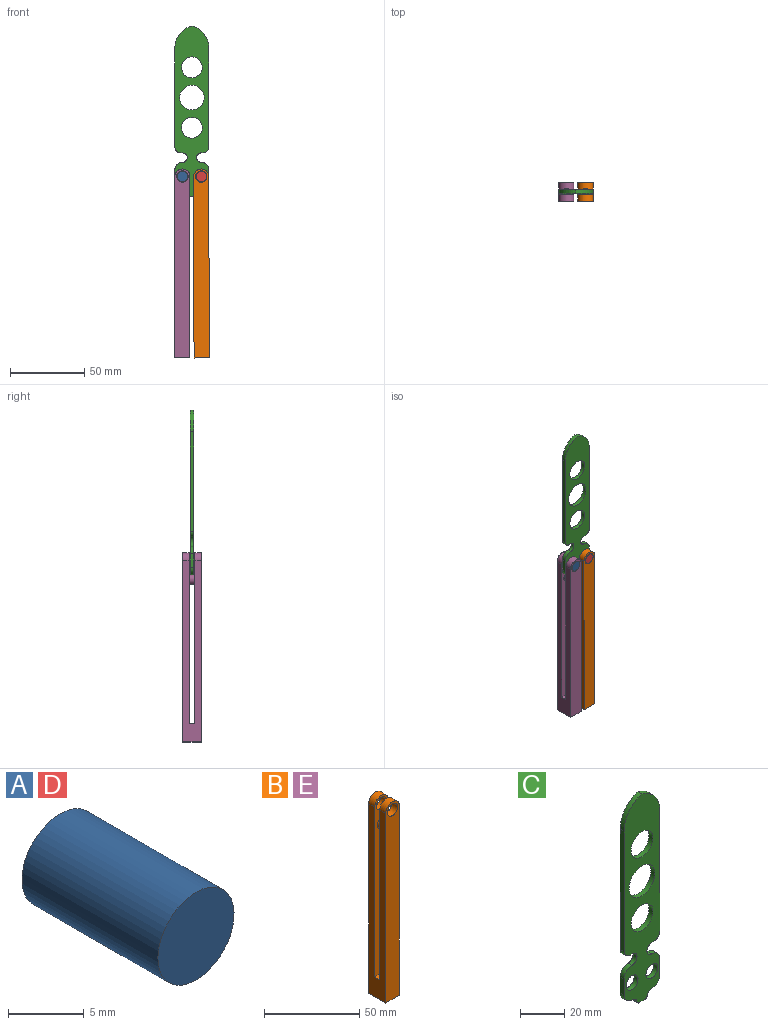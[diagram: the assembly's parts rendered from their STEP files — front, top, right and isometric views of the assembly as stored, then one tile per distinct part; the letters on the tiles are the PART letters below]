
ASSEMBLY  parts=5 mates=4
PART A: 3 faces, bbox 7.1x12.7x7.1 mm
  f0: cylinder r=3.56mm len=12.7mm, axis (0,-1,0), area 283.8mm2, adj f1,f2
  f1: plane 7.11x7.11mm, normal (0,1,0), area 39.7mm2, adj f0
  f2: plane 7.11x7.11mm, normal (0,-1,0), area 39.7mm2, adj f0
PART B: 13 faces, bbox 10.2x12.7x127 mm
  f0: plane 12.7x10.16mm, normal (0,0,-1), area 129mm2, adj f1,f2,f8,f9
  f1: plane 127x10.16mm, normal (0,1,0), area 1233.6mm2, adj f0,f7,f8,f9,f10
  f2: plane 127x10.16mm, normal (0,-1,0), area 1233.6mm2, adj f0,f6,f8,f9,f11
  f3: plane 114.3x10.16mm, normal (0,-1,0), area 1072.9mm2, adj f5,f7,f8,f9,f10,f12
  f4: plane 114.3x10.16mm, normal (0,1,0), area 1072.9mm2, adj f5,f6,f8,f9,f11,f12
  f5: plane 10.16x3.81mm, normal (0,0,1), area 38.7mm2, adj f3,f4,f8,f9
  f6: cylinder r=3.81mm len=7.62mm, axis (0,-1,0), area 106.4mm2, adj f2,f4
  f7: cylinder r=3.81mm len=7.62mm, axis (0,-1,0), area 106.4mm2, adj f1,f3
  f8: plane 121.92x12.7mm, normal (1,0,0), area 1132.3mm2, adj f0,f1,f2,f3,f4,f5,f10,f11
  f9: plane 121.92x12.7mm, normal (-1,0,0), area 1132.3mm2, adj f0,f1,f2,f3,f4,f5,f10,f11
  f10: cylinder r=5.08mm len=10.16mm, axis (0,1,0), area 70.9mm2, adj f1,f3,f8,f9
  f11: cylinder r=5.08mm len=10.16mm, axis (0,-1,0), area 70.9mm2, adj f2,f4,f8,f9
  f12: cylinder r=3.17mm len=6.35mm, axis (0,-1,0), area 76mm2, adj f3,f4
PART C: 28 faces, bbox 22.9x2.5x114.5 mm
  f0: cylinder r=3.17mm len=3.14mm, axis (0,-1,0), area 11.5mm2, adj f3,f4,f17,f20
  f1: plane 8.89x2.54mm, normal (-1,0,0), area 22.6mm2, adj f3,f4,f19,f22
  f2: plane 8.89x2.54mm, normal (1,0,0), area 22.6mm2, adj f3,f4,f20,f21
  f3: plane 114.45x22.86mm, normal (0,1,0), area 1733.4mm2, adj f0,f1,f2,f5,f6,f7,f8,f9
  f4: plane 114.45x22.86mm, normal (0,-1,0), area 1733.4mm2, adj f0,f1,f2,f5,f6,f7,f8,f9
  f5: plane 66.68x2.54mm, normal (-1,0,0), area 169.4mm2, adj f3,f4,f7,f24
  f6: plane 66.68x2.54mm, normal (1,0,0), area 169.4mm2, adj f3,f4,f8,f23
  f7: cylinder r=15.24mm len=14.76mm, axis (0,-1,0), area 51mm2, adj f3,f4,f5,f8
  f8: cylinder r=15.24mm len=14.76mm, axis (0,1,0), area 51mm2, adj f3,f4,f6,f7
  f9: cylinder r=3.81mm len=7.62mm, axis (0,-1,0), area 60.8mm2, adj f3,f4
  f10: cylinder r=3.81mm len=7.62mm, axis (0,-1,0), area 60.8mm2, adj f3,f4
  f11: plane 2.54x1.27mm, normal (0,0,-1), area 3.2mm2, adj f3,f4,f12,f24
  f12: cylinder r=3.17mm len=6.35mm, axis (0,-1,0), area 25.3mm2, adj f3,f4,f11,f22
  f13: plane 2.54x1.27mm, normal (0,0,-1), area 3.2mm2, adj f3,f4,f14,f23
  f14: cylinder r=3.17mm len=6.35mm, axis (0,-1,0), area 25.3mm2, adj f3,f4,f13,f21
  f15: cylinder r=3.17mm len=3.14mm, axis (0,-1,0), area 11.5mm2, adj f3,f4,f18,f19
  f16: plane 3.9x2.54mm, normal (0,0,-1), area 9.9mm2, adj f3,f4,f17,f18
  f17: cylinder r=1.27mm len=2.54mm, axis (0,-1,0), area 4.6mm2, adj f0,f3,f4,f16
  f18: cylinder r=1.27mm len=2.54mm, axis (0,-1,0), area 4.6mm2, adj f3,f4,f15,f16
  f19: cylinder r=5.08mm len=5.08mm, axis (0,-1,0), area 20.3mm2, adj f1,f3,f4,f15
  f20: cylinder r=5.08mm len=5.08mm, axis (0,-1,0), area 20.3mm2, adj f0,f2,f3,f4
  f21: cylinder r=5.08mm len=5.08mm, axis (0,1,0), area 20.3mm2, adj f2,f3,f4,f14
  f22: cylinder r=5.08mm len=5.08mm, axis (0,1,0), area 20.3mm2, adj f1,f3,f4,f12
  f23: cylinder r=3.81mm len=3.81mm, axis (0,-1,0), area 15.2mm2, adj f3,f4,f6,f13
  f24: cylinder r=3.81mm len=3.81mm, axis (0,-1,0), area 15.2mm2, adj f3,f4,f5,f11
  f25: cylinder r=6.99mm len=13.97mm, axis (0,-1,0), area 111.5mm2, adj f3,f4
  f26: cylinder r=8.26mm len=16.51mm, axis (0,-1,0), area 131.7mm2, adj f3,f4
  f27: cylinder r=6.99mm len=13.97mm, axis (0,-1,0), area 111.5mm2, adj f3,f4
PART D: same geometry as A
PART E: same geometry as B
PLACE A t=(20.78,1.06,12.73)mm
PLACE B rot(axis=(0,-1,0),0.1deg) t=(26.04,1.06,-109.2)mm
PLACE C t=(15.7,6.14,12.73)mm fixed
PLACE D t=(33.48,1.06,12.73)mm
PLACE E t=(13.16,1.06,-109.19)mm
MATE fastened D.f0 <-> C.f9  axis (0,-1,0) through (33.48,7.41,12.73)mm
MATE fastened A.f0 <-> C.f10  axis (0,-1,0) through (20.78,7.41,12.73)mm
MATE revolute B.f6 <-> D.f0  axis (0,-1,0) through (33.48,1.06,12.73)mm
MATE revolute E.f6 <-> A.f0  axis (0,-1,0) through (20.78,1.06,12.73)mm
